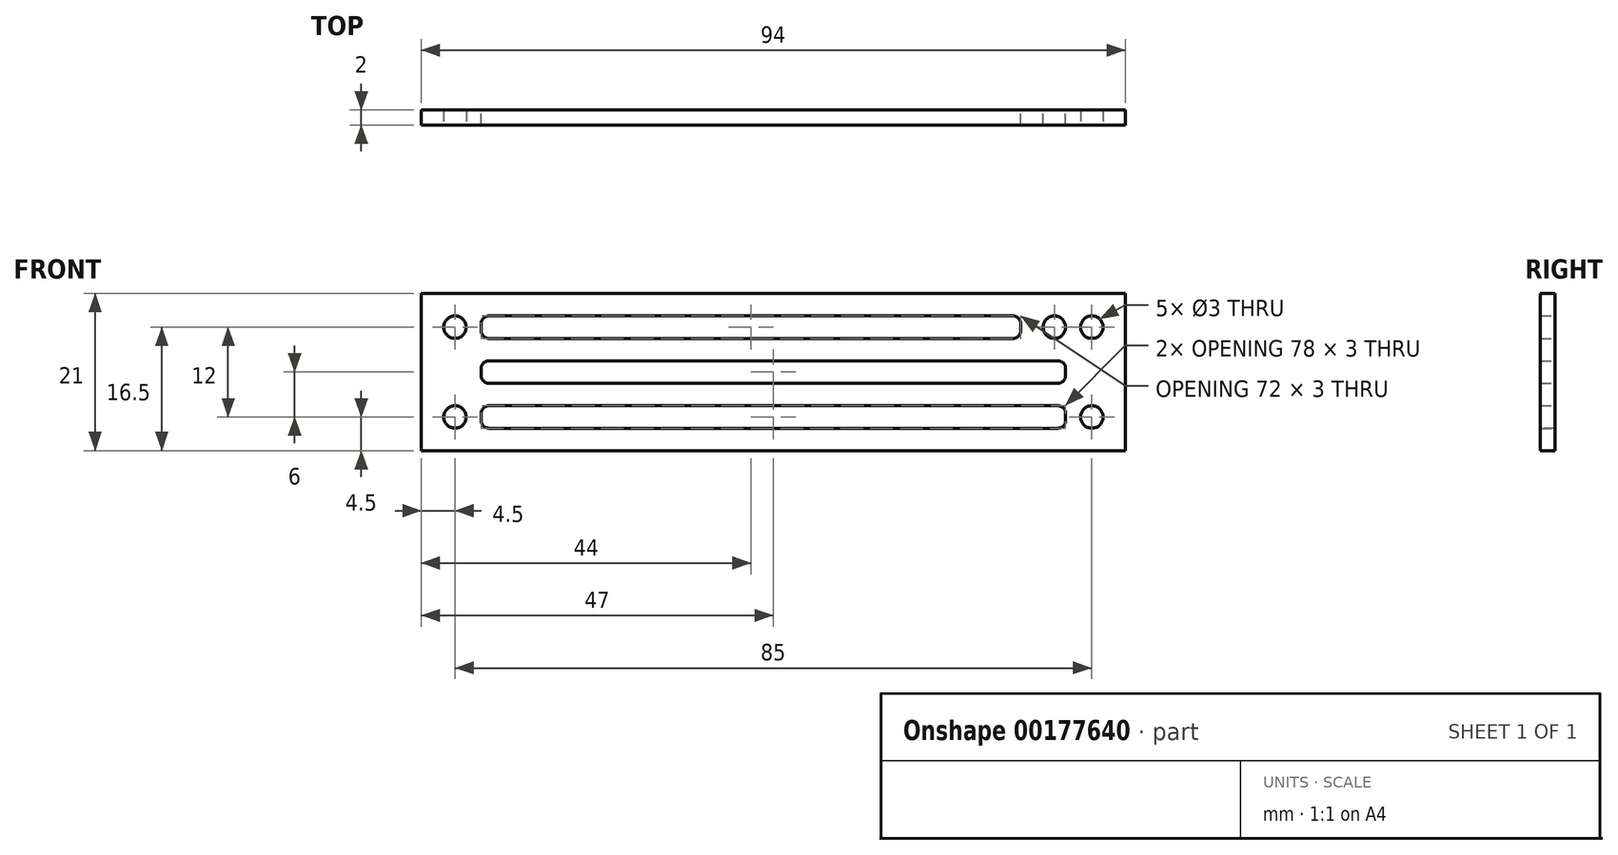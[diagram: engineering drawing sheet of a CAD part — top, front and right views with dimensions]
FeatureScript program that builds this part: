
annotation { "Feature Type Name" : "Feature", "Feature Type Description" : "" }
export const myFeature = defineFeature(function(context is Context, id is Id, definition is map)
    precondition{}
    {
        {
            var Q0;
            Q0=qCreatedBy(makeId("Front.planeOp"),FACE);
            var sketch = newSketch(context, id + "F0", { "sketchPlane" : qUnion([Q0])});
            skLineSegment(sketch, "E0.bottom", {"start": v(42, 10.5) * mm, "end": v(-42, 10.5) * mm});
            skLineSegment(sketch, "E0.top", {"start": v(42, -10.5) * mm, "end": v(-42, -10.5) * mm});
            skLineSegment(sketch, "E0.left", {"start": v(42, 10.5) * mm, "end": v(42, -10.5) * mm});
            skLineSegment(sketch, "E0.right", {"start": v(-42, 10.5) * mm, "end": v(-42, -10.5) * mm});
            skPoint(sketch, "E0.middle", {"position": v(0, 0) * mm});
            skLineSegment(sketch, "E1.bottom", {"start": v(39, -4.5) * mm, "end": v(-39, -4.5) * mm});
            skLineSegment(sketch, "E1.top", {"start": v(39, -7.5) * mm, "end": v(-39, -7.5) * mm});
            skLineSegment(sketch, "E1.left", {"start": v(39, -4.5) * mm, "end": v(39, -7.5) * mm});
            skLineSegment(sketch, "E1.right", {"start": v(-39, -4.5) * mm, "end": v(-39, -7.5) * mm});
            skPoint(sketch, "E1.middle", {"position": v(0, -6) * mm});
            skLineSegment(sketch, "E2.bottom", {"start": v(39, 1.5) * mm, "end": v(-39, 1.5) * mm});
            skLineSegment(sketch, "E2.top", {"start": v(39, -1.5) * mm, "end": v(-39, -1.5) * mm});
            skLineSegment(sketch, "E2.left", {"start": v(39, 1.5) * mm, "end": v(39, -1.5) * mm});
            skLineSegment(sketch, "E2.right", {"start": v(-39, 1.5) * mm, "end": v(-39, -1.5) * mm});
            skLineSegment(sketch, "E3.bottom", {"start": v(-39, 7.5) * mm, "end": v(33, 7.5) * mm});
            skLineSegment(sketch, "E3.top", {"start": v(-39, 4.5) * mm, "end": v(33, 4.5) * mm});
            skLineSegment(sketch, "E3.left", {"start": v(-39, 7.5) * mm, "end": v(-39, 4.5) * mm});
            skLineSegment(sketch, "E3.right", {"start": v(33, 7.5) * mm, "end": v(33, 4.5) * mm});
            skCircle(sketch, "E4", {"center": v(37.5, 6) * mm, "radius": 1.5 * mm});
            skSolve(sketch);
        }
        {
            var Q0;
            Q0 = qSketchRegion(id + "F0", true);
            extrude(context, id + "F1", {"entities" : qUnion([Q0]), "depth" : 2 * mm});
        }
        {
            var Q0;
            Q0=makeQuery(id+"F1.opExtrude","SWEPT_FACE",FACE,{"disambiguationData":[OSD([sQuery(id+"F0.wireOp",EDGE,"E0.left")])]});
            var sketch = newSketch(context, id + "F2", { "sketchPlane" : qUnion([Q0])});
            skLineSegment(sketch, "E5.bottom", {"start": v(-2, 10.5) * mm, "end": v(0, 10.5) * mm});
            skLineSegment(sketch, "E5.top", {"start": v(-2, -10.5) * mm, "end": v(0, -10.5) * mm});
            skLineSegment(sketch, "E5.left", {"start": v(-2, 10.5) * mm, "end": v(-2, -10.5) * mm});
            skLineSegment(sketch, "E5.right", {"start": v(0, 10.5) * mm, "end": v(0, -10.5) * mm});
            skSolve(sketch);
        }
        {
            var Q0;
            Q0 = qSketchRegion(id + "F2", true);
            extrude(context, id + "F3", {"entities" : qUnion([Q0]), "operationType" : NewBodyOperationType.ADD, "depth" : 5 * mm});
        }
        {
            var Q0;
            Q0=makeQuery(id+"F1.opExtrude","SWEPT_FACE",FACE,{"disambiguationData":[OSD([sQuery(id+"F0.wireOp",EDGE,"E0.right")])]});
            var sketch = newSketch(context, id + "F4", { "sketchPlane" : qUnion([Q0])});
            skLineSegment(sketch, "E6.bottom", {"start": v(0, 10.5) * mm, "end": v(2, 10.5) * mm});
            skLineSegment(sketch, "E6.top", {"start": v(0, -10.5) * mm, "end": v(2, -10.5) * mm});
            skLineSegment(sketch, "E6.left", {"start": v(0, 10.5) * mm, "end": v(0, -10.5) * mm});
            skLineSegment(sketch, "E6.right", {"start": v(2, 10.5) * mm, "end": v(2, -10.5) * mm});
            skSolve(sketch);
        }
        {
            var Q0;
            Q0 = qSketchRegion(id + "F4", true);
            extrude(context, id + "F5", {"entities" : qUnion([Q0]), "operationType" : NewBodyOperationType.ADD, "depth" : 5 * mm});
        }
        {
            var Q0;
            Q0=makeQuery(id+"F5.boolean.opBoolean","MERGE",FACE,{"derivedFrom":[makeQuery(id+"F3.boolean.opBoolean","MERGE",FACE,{"derivedFrom":[makeQuery(id+"F1.opExtrude","CAP_FACE",FACE,{"disambiguationData":[OSD([sQuery(id+"F0.wireOp",EDGE,"E0.bottom"),sQuery(id+"F0.wireOp",EDGE,"E0.top"),sQuery(id+"F0.wireOp",EDGE,"E0.left"),sQuery(id+"F0.wireOp",EDGE,"E0.right"),sQuery(id+"F0.wireOp",EDGE,"E1.bottom"),sQuery(id+"F0.wireOp",EDGE,"E1.top"),sQuery(id+"F0.wireOp",EDGE,"E1.left"),sQuery(id+"F0.wireOp",EDGE,"E1.right"),sQuery(id+"F0.wireOp",EDGE,"E2.bottom"),sQuery(id+"F0.wireOp",EDGE,"E2.top"),sQuery(id+"F0.wireOp",EDGE,"E2.left"),sQuery(id+"F0.wireOp",EDGE,"E2.right"),sQuery(id+"F0.wireOp",EDGE,"E3.bottom"),sQuery(id+"F0.wireOp",EDGE,"E3.top"),sQuery(id+"F0.wireOp",EDGE,"E3.left"),sQuery(id+"F0.wireOp",EDGE,"E3.right"),sQuery(id+"F0.wireOp",EDGE,"E4")])],"isStart":false}),makeQuery(id+"F3.opExtrude","SWEPT_FACE",FACE,{"disambiguationData":[OSD([sQuery(id+"F2.wireOp",EDGE,"E5.left")])]})]}),makeQuery(id+"F5.opExtrude","SWEPT_FACE",FACE,{"disambiguationData":[OSD([sQuery(id+"F4.wireOp",EDGE,"E6.right")])]})]});
            var sketch = newSketch(context, id + "F6", { "sketchPlane" : qUnion([Q0])});
            skCircle(sketch, "E7", {"center": v(-42.5, 6) * mm, "radius": 1.5 * mm});
            skCircle(sketch, "E8", {"center": v(-42.5, -6) * mm, "radius": 1.5 * mm});
            skCircle(sketch, "E9", {"center": v(42.5, 6) * mm, "radius": 1.5 * mm});
            skCircle(sketch, "E10", {"center": v(42.5, -6) * mm, "radius": 1.5 * mm});
            skSolve(sketch);
        }
        {
            var Q0;
            Q0 = qSketchRegion(id + "F6", true);
            extrude(context, id + "F7", {"entities" : qUnion([Q0]), "operationType" : NewBodyOperationType.REMOVE, "oppositeDirection" : true, "depth" : 25 * mm});
        }
        {
            var Q0;
            Q0=makeQuery(id+"F1.opExtrude","SWEPT_EDGE",EDGE,{"disambiguationData":[OSD([sQuery(id+"F0.wireOp",EDGE,"E3.bottom"),sQuery(id+"F0.wireOp",EDGE,"E3.left")])]});
            var Q1;
            Q1=makeQuery(id+"F1.opExtrude","SWEPT_EDGE",EDGE,{"disambiguationData":[OSD([sQuery(id+"F0.wireOp",EDGE,"E2.bottom"),sQuery(id+"F0.wireOp",EDGE,"E2.right")])]});
            var Q2;
            Q2=makeQuery(id+"F1.opExtrude","SWEPT_EDGE",EDGE,{"disambiguationData":[OSD([sQuery(id+"F0.wireOp",EDGE,"E1.bottom"),sQuery(id+"F0.wireOp",EDGE,"E1.right")])]});
            var Q3;
            Q3=makeQuery(id+"F1.opExtrude","SWEPT_EDGE",EDGE,{"disambiguationData":[OSD([sQuery(id+"F0.wireOp",EDGE,"E3.top"),sQuery(id+"F0.wireOp",EDGE,"E3.left")])]});
            var Q4;
            Q4=makeQuery(id+"F1.opExtrude","SWEPT_EDGE",EDGE,{"disambiguationData":[OSD([sQuery(id+"F0.wireOp",EDGE,"E2.top"),sQuery(id+"F0.wireOp",EDGE,"E2.right")])]});
            var Q5;
            Q5=makeQuery(id+"F1.opExtrude","SWEPT_EDGE",EDGE,{"disambiguationData":[OSD([sQuery(id+"F0.wireOp",EDGE,"E1.top"),sQuery(id+"F0.wireOp",EDGE,"E1.right")])]});
            var Q6;
            Q6=makeQuery(id+"F1.opExtrude","SWEPT_EDGE",EDGE,{"disambiguationData":[OSD([sQuery(id+"F0.wireOp",EDGE,"E3.bottom"),sQuery(id+"F0.wireOp",EDGE,"E3.right")])]});
            var Q7;
            Q7=makeQuery(id+"F1.opExtrude","SWEPT_EDGE",EDGE,{"disambiguationData":[OSD([sQuery(id+"F0.wireOp",EDGE,"E2.bottom"),sQuery(id+"F0.wireOp",EDGE,"E2.left")])]});
            var Q8;
            Q8=makeQuery(id+"F1.opExtrude","SWEPT_EDGE",EDGE,{"disambiguationData":[OSD([sQuery(id+"F0.wireOp",EDGE,"E1.bottom"),sQuery(id+"F0.wireOp",EDGE,"E1.left")])]});
            var Q9;
            Q9=makeQuery(id+"F1.opExtrude","SWEPT_EDGE",EDGE,{"disambiguationData":[OSD([sQuery(id+"F0.wireOp",EDGE,"E1.top"),sQuery(id+"F0.wireOp",EDGE,"E1.left")])]});
            var Q10;
            Q10=makeQuery(id+"F1.opExtrude","SWEPT_EDGE",EDGE,{"disambiguationData":[OSD([sQuery(id+"F0.wireOp",EDGE,"E2.top"),sQuery(id+"F0.wireOp",EDGE,"E2.left")])]});
            var Q11;
            Q11=makeQuery(id+"F1.opExtrude","SWEPT_EDGE",EDGE,{"disambiguationData":[OSD([sQuery(id+"F0.wireOp",EDGE,"E3.top"),sQuery(id+"F0.wireOp",EDGE,"E3.right")])]});
            fillet(context, id + "F8", {"entities" : qUnion([Q0, Q1, Q2, Q3, Q4, Q5, Q6, Q7, Q8, Q9, Q10, Q11]), "radius" : 1 * mm, "tangentPropagation" : true, "allowEdgeOverflow" : false});
        }
    });
